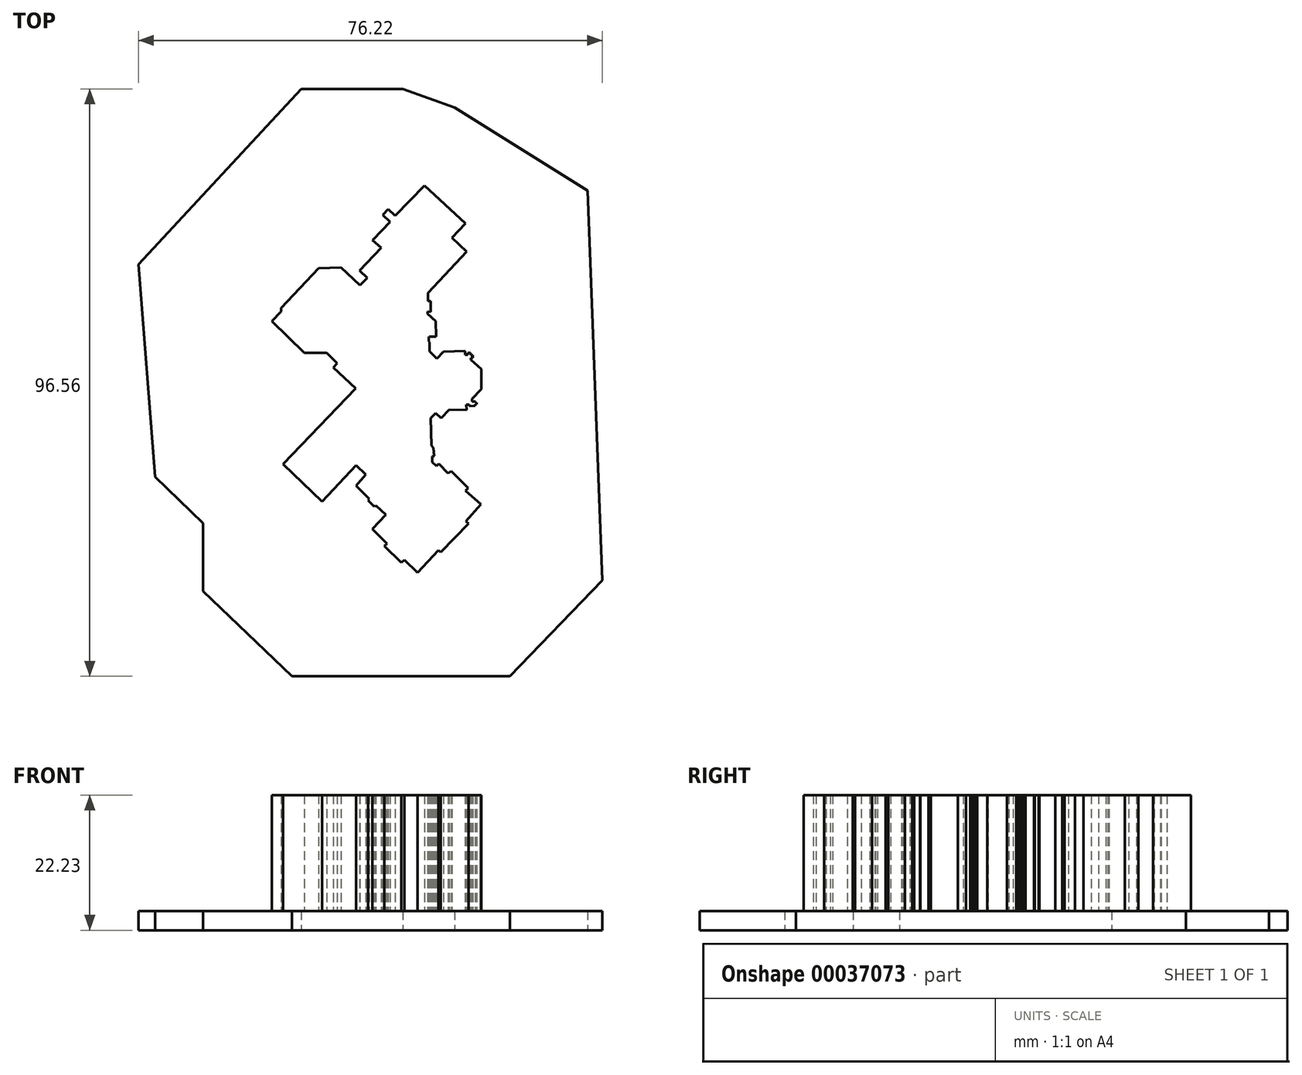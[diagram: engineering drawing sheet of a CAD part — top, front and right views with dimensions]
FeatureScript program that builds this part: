
annotation { "Feature Type Name" : "Feature", "Feature Type Description" : "" }
export const myFeature = defineFeature(function(context is Context, id is Id, definition is map)
    precondition{}
    {
        {
            var Q0;
            Q0=qCreatedBy(makeId("Top.planeOp"),FACE);
            var sketch = newSketch(context, id + "F0", { "sketchPlane" : qUnion([Q0])});
            skLineSegment(sketch, "E0", {"start": v(-23.08, 49.34) * mm, "end": v(-6.38, 49.34) * mm});
            skLineSegment(sketch, "E1", {"start": v(-6.38, 49.34) * mm, "end": v(2.13, 46.3) * mm});
            skLineSegment(sketch, "E2", {"start": v(2.13, 46.3) * mm, "end": v(23.99, 32.64) * mm});
            skLineSegment(sketch, "E3", {"start": v(23.99, 32.64) * mm, "end": v(26.42, -31.43) * mm});
            skLineSegment(sketch, "E4", {"start": v(26.42, -31.43) * mm, "end": v(11.23, -47.22) * mm});
            skLineSegment(sketch, "E5", {"start": v(11.23, -47.22) * mm, "end": v(-24.6, -47.22) * mm});
            skLineSegment(sketch, "E6", {"start": v(-24.6, -47.22) * mm, "end": v(-39.17, -33.25) * mm});
            skLineSegment(sketch, "E7", {"start": v(-39.17, -33.25) * mm, "end": v(-39.17, -22.01) * mm});
            skLineSegment(sketch, "E8", {"start": v(-39.17, -22.01) * mm, "end": v(-47.06, -14.42) * mm});
            skLineSegment(sketch, "E9", {"start": v(-47.06, -14.42) * mm, "end": v(-49.8, 20.5) * mm});
            skLineSegment(sketch, "E10", {"start": v(-49.8, 20.5) * mm, "end": v(-23.08, 49.34) * mm});
            skSolve(sketch);
        }
        {
            var Q0;
            Q0=makeQuery(id+"F0.imprint","IMPRINT",FACE,{"disambiguationData":[TD([[makeQuery(id+"F0.imprint","IMPRINT",EDGE,{"derivedFrom":sQuery(id+"F0.wireOp",EDGE,"E0")}),-1.0]])]});
            extrude(context, id + "F1", {"entities" : qUnion([Q0]), "depth" : 3.17 * mm});
        }
        {
            var Q0;
            Q0=makeQuery(id+"F1.opExtrude","CAP_FACE",FACE,{"disambiguationData":[OSD([sQuery(id+"F0.wireOp",EDGE,"E0"),sQuery(id+"F0.wireOp",EDGE,"E1"),sQuery(id+"F0.wireOp",EDGE,"E2"),sQuery(id+"F0.wireOp",EDGE,"E3"),sQuery(id+"F0.wireOp",EDGE,"E4"),sQuery(id+"F0.wireOp",EDGE,"E5"),sQuery(id+"F0.wireOp",EDGE,"E6"),sQuery(id+"F0.wireOp",EDGE,"E7"),sQuery(id+"F0.wireOp",EDGE,"E8"),sQuery(id+"F0.wireOp",EDGE,"E9"),sQuery(id+"F0.wireOp",EDGE,"E10")])],"isStart":false});
            var sketch = newSketch(context, id + "F2", { "sketchPlane" : qUnion([Q0])});
            skLineSegment(sketch, "E11", {"start": v(-11.23, 24.6) * mm, "end": v(-8.46, 27.47) * mm});
            skLineSegment(sketch, "E12", {"start": v(-8.46, 27.47) * mm, "end": v(-9.65, 28.61) * mm});
            skLineSegment(sketch, "E13", {"start": v(-9.65, 28.61) * mm, "end": v(-8.75, 29.55) * mm});
            skLineSegment(sketch, "E14", {"start": v(-8.75, 29.55) * mm, "end": v(-7.63, 28.48) * mm});
            skLineSegment(sketch, "E15", {"start": v(-7.63, 28.48) * mm, "end": v(-2.82, 33.47) * mm});
            skLineSegment(sketch, "E16", {"start": v(-2.82, 33.47) * mm, "end": v(3.93, 27.23) * mm});
            skLineSegment(sketch, "E17", {"start": v(3.93, 27.23) * mm, "end": v(1.74, 24.86) * mm});
            skLineSegment(sketch, "E18", {"start": v(1.74, 24.86) * mm, "end": v(4.13, 22.62) * mm});
            skLineSegment(sketch, "E19", {"start": v(4.13, 22.62) * mm, "end": v(-2.23, 15.81) * mm});
            skLineSegment(sketch, "E20", {"start": v(-2.23, 15.81) * mm, "end": v(-2.23, 14.44) * mm});
            skLineSegment(sketch, "E21", {"start": v(-2.23, 14.44) * mm, "end": v(-1.8, 14.44) * mm});
            skLineSegment(sketch, "E22", {"start": v(-1.8, 14.44) * mm, "end": v(-1.8, 12.7) * mm});
            skLineSegment(sketch, "E23", {"start": v(-1.8, 12.7) * mm, "end": v(-2.3, 12.75) * mm});
            skLineSegment(sketch, "E24", {"start": v(-2.3, 12.75) * mm, "end": v(-2.3, 12.35) * mm});
            skLineSegment(sketch, "E25", {"start": v(-2.3, 12.35) * mm, "end": v(-0.95, 11.18) * mm});
            skLineSegment(sketch, "E26", {"start": v(-0.95, 11.18) * mm, "end": v(-0.88, 8.63) * mm});
            skLineSegment(sketch, "E27", {"start": v(-0.88, 8.63) * mm, "end": v(-2.02, 8.6) * mm});
            skLineSegment(sketch, "E28", {"start": v(-2.02, 8.6) * mm, "end": v(-2.13, 8.49) * mm});
            skLineSegment(sketch, "E29", {"start": v(-2.13, 8.49) * mm, "end": v(-2.13, 7.83) * mm});
            skLineSegment(sketch, "E30", {"start": v(-2.13, 7.83) * mm, "end": v(-1.99, 7.7) * mm});
            skLineSegment(sketch, "E31", {"start": v(-1.99, 7.7) * mm, "end": v(-1.99, 6.24) * mm});
            skLineSegment(sketch, "E32", {"start": v(-1.99, 6.24) * mm, "end": v(-0.74, 5.03) * mm});
            skLineSegment(sketch, "E33", {"start": v(-0.74, 5.03) * mm, "end": v(0.32, 6.13) * mm});
            skLineSegment(sketch, "E34", {"start": v(0.32, 6.13) * mm, "end": v(3.84, 6.3) * mm});
            skLineSegment(sketch, "E35", {"start": v(3.84, 6.3) * mm, "end": v(3.88, 5.65) * mm});
            skLineSegment(sketch, "E36", {"start": v(3.88, 5.65) * mm, "end": v(4.32, 5.66) * mm});
            skLineSegment(sketch, "E37", {"start": v(4.32, 5.66) * mm, "end": v(4.32, 5.93) * mm});
            skLineSegment(sketch, "E38", {"start": v(4.32, 5.93) * mm, "end": v(4.79, 5.94) * mm});
            skLineSegment(sketch, "E39", {"start": v(4.79, 5.94) * mm, "end": v(4.8, 5.56) * mm});
            skLineSegment(sketch, "E40", {"start": v(4.8, 5.56) * mm, "end": v(5.15, 5.56) * mm});
            skLineSegment(sketch, "E41", {"start": v(5.15, 5.56) * mm, "end": v(5.15, 5.14) * mm});
            skLineSegment(sketch, "E42", {"start": v(5.15, 5.14) * mm, "end": v(4.85, 5.14) * mm});
            skLineSegment(sketch, "E43", {"start": v(4.85, 5.14) * mm, "end": v(4.85, 4.79) * mm});
            skLineSegment(sketch, "E44", {"start": v(4.85, 4.79) * mm, "end": v(6.54, 3.26) * mm});
            skLineSegment(sketch, "E45", {"start": v(6.54, 3.26) * mm, "end": v(6.54, 0) * mm});
            skLineSegment(sketch, "E46", {"start": v(6.54, 0) * mm, "end": v(5.01, -1.63) * mm});
            skLineSegment(sketch, "E47", {"start": v(5.01, -1.63) * mm, "end": v(5.01, -2.04) * mm});
            skLineSegment(sketch, "E48", {"start": v(5.01, -2.04) * mm, "end": v(5.58, -2.02) * mm});
            skLineSegment(sketch, "E49", {"start": v(5.58, -2.02) * mm, "end": v(5.59, -2.22) * mm});
            skLineSegment(sketch, "E50", {"start": v(5.59, -2.22) * mm, "end": v(5.78, -2.2) * mm});
            skLineSegment(sketch, "E51", {"start": v(5.78, -2.2) * mm, "end": v(5.79, -2.5) * mm});
            skLineSegment(sketch, "E52", {"start": v(5.79, -2.5) * mm, "end": v(5.53, -2.5) * mm});
            skLineSegment(sketch, "E53", {"start": v(5.53, -2.5) * mm, "end": v(5.53, -2.76) * mm});
            skLineSegment(sketch, "E54", {"start": v(5.53, -2.76) * mm, "end": v(4.55, -2.8) * mm});
            skLineSegment(sketch, "E55", {"start": v(4.55, -2.8) * mm, "end": v(4.54, -2.55) * mm});
            skLineSegment(sketch, "E56", {"start": v(4.54, -2.55) * mm, "end": v(4.1, -2.56) * mm});
            skLineSegment(sketch, "E57", {"start": v(4.1, -2.56) * mm, "end": v(4.12, -3.46) * mm});
            skLineSegment(sketch, "E58", {"start": v(4.12, -3.46) * mm, "end": v(1.28, -3.39) * mm});
            skLineSegment(sketch, "E59", {"start": v(1.28, -3.39) * mm, "end": v(-0.08, -4.79) * mm});
            skLineSegment(sketch, "E60", {"start": v(-0.08, -4.79) * mm, "end": v(-0.96, -3.94) * mm});
            skLineSegment(sketch, "E61", {"start": v(-0.96, -3.94) * mm, "end": v(-1.76, -4.75) * mm});
            skLineSegment(sketch, "E62", {"start": v(-1.76, -4.75) * mm, "end": v(-1.64, -9.28) * mm});
            skLineSegment(sketch, "E63", {"start": v(-1.64, -9.28) * mm, "end": v(-1.32, -9.64) * mm});
            skLineSegment(sketch, "E64", {"start": v(-1.32, -9.64) * mm, "end": v(-1.21, -11) * mm});
            skLineSegment(sketch, "E65", {"start": v(-1.21, -11) * mm, "end": v(-1.51, -11.05) * mm});
            skLineSegment(sketch, "E66", {"start": v(-1.51, -11.05) * mm, "end": v(-1.51, -12) * mm});
            skLineSegment(sketch, "E67", {"start": v(-1.51, -12) * mm, "end": v(-0.81, -12.66) * mm});
            skLineSegment(sketch, "E68", {"start": v(-0.81, -12.66) * mm, "end": v(-0.45, -12.3) * mm});
            skLineSegment(sketch, "E69", {"start": v(-0.45, -12.3) * mm, "end": v(1.1, -13.84) * mm});
            skLineSegment(sketch, "E70", {"start": v(1.1, -13.84) * mm, "end": v(1.6, -13.5) * mm});
            skLineSegment(sketch, "E71", {"start": v(1.6, -13.5) * mm, "end": v(4.36, -16.25) * mm});
            skLineSegment(sketch, "E72", {"start": v(4.36, -16.25) * mm, "end": v(3.96, -16.7) * mm});
            skLineSegment(sketch, "E73", {"start": v(3.96, -16.7) * mm, "end": v(6.46, -18.91) * mm});
            skLineSegment(sketch, "E74", {"start": v(6.46, -18.91) * mm, "end": v(3.98, -21.7) * mm});
            skLineSegment(sketch, "E75", {"start": v(3.98, -21.7) * mm, "end": v(4.41, -22.09) * mm});
            skLineSegment(sketch, "E76", {"start": v(4.41, -22.09) * mm, "end": v(-0.1, -26.8) * mm});
            skLineSegment(sketch, "E77", {"start": v(-0.1, -26.8) * mm, "end": v(-0.5, -26.47) * mm});
            skLineSegment(sketch, "E78", {"start": v(-0.5, -26.47) * mm, "end": v(-3.92, -30.15) * mm});
            skLineSegment(sketch, "E79", {"start": v(-3.92, -30.15) * mm, "end": v(-6.12, -28.1) * mm});
            skLineSegment(sketch, "E80", {"start": v(-6.12, -28.1) * mm, "end": v(-6.61, -28.54) * mm});
            skLineSegment(sketch, "E81", {"start": v(-6.61, -28.54) * mm, "end": v(-9.37, -25.76) * mm});
            skLineSegment(sketch, "E82", {"start": v(-9.37, -25.76) * mm, "end": v(-8.97, -25.4) * mm});
            skLineSegment(sketch, "E83", {"start": v(-8.97, -25.4) * mm, "end": v(-11.38, -22.99) * mm});
            skLineSegment(sketch, "E84", {"start": v(-11.38, -22.99) * mm, "end": v(-9.16, -20.66) * mm});
            skLineSegment(sketch, "E85", {"start": v(-9.16, -20.66) * mm, "end": v(-10.8, -19.1) * mm});
            skLineSegment(sketch, "E86", {"start": v(-10.8, -19.1) * mm, "end": v(-11.04, -19.3) * mm});
            skLineSegment(sketch, "E87", {"start": v(-11.04, -19.3) * mm, "end": v(-12.05, -18.32) * mm});
            skLineSegment(sketch, "E88", {"start": v(-12.05, -18.32) * mm, "end": v(-11.84, -18.04) * mm});
            skLineSegment(sketch, "E89", {"start": v(-11.84, -18.04) * mm, "end": v(-14.06, -15.87) * mm});
            skLineSegment(sketch, "E90", {"start": v(-14.06, -15.87) * mm, "end": v(-12.45, -14.07) * mm});
            skLineSegment(sketch, "E91", {"start": v(-12.45, -14.07) * mm, "end": v(-14.04, -12.54) * mm});
            skLineSegment(sketch, "E92", {"start": v(-14.04, -12.54) * mm, "end": v(-19.64, -18.49) * mm});
            skLineSegment(sketch, "E93", {"start": v(-19.64, -18.49) * mm, "end": v(-26, -12.36) * mm});
            skLineSegment(sketch, "E94", {"start": v(-26, -12.36) * mm, "end": v(-14.11, 0.13) * mm});
            skLineSegment(sketch, "E95", {"start": v(-14.11, 0.13) * mm, "end": v(-17.8, 3.56) * mm});
            skLineSegment(sketch, "E96", {"start": v(-17.8, 3.56) * mm, "end": v(-17.14, 4.27) * mm});
            skLineSegment(sketch, "E97", {"start": v(-17.14, 4.27) * mm, "end": v(-18.85, 5.93) * mm});
            skLineSegment(sketch, "E98", {"start": v(-18.85, 5.93) * mm, "end": v(-22.52, 5.93) * mm});
            skLineSegment(sketch, "E99", {"start": v(-22.52, 5.93) * mm, "end": v(-27.89, 11.14) * mm});
            skLineSegment(sketch, "E100", {"start": v(-27.89, 11.14) * mm, "end": v(-26.32, 12.76) * mm});
            skLineSegment(sketch, "E101", {"start": v(-26.32, 12.76) * mm, "end": v(-26.36, 13.33) * mm});
            skLineSegment(sketch, "E102", {"start": v(-26.36, 13.33) * mm, "end": v(-20.17, 19.86) * mm});
            skLineSegment(sketch, "E103", {"start": v(-20.17, 19.86) * mm, "end": v(-16.54, 20) * mm});
            skLineSegment(sketch, "E104", {"start": v(-16.54, 20) * mm, "end": v(-13.4, 17.1) * mm});
            skLineSegment(sketch, "E105", {"start": v(-13.4, 17.1) * mm, "end": v(-12.22, 18.29) * mm});
            skLineSegment(sketch, "E106", {"start": v(-12.22, 18.29) * mm, "end": v(-13.44, 19.5) * mm});
            skLineSegment(sketch, "E107", {"start": v(-13.44, 19.5) * mm, "end": v(-9.91, 23.24) * mm});
            skLineSegment(sketch, "E108", {"start": v(-9.91, 23.24) * mm, "end": v(-11.35, 24.52) * mm});
            skLineSegment(sketch, "E109", {"start": v(-11.35, 24.52) * mm, "end": v(-11.23, 24.6) * mm});
            skSolve(sketch);
        }
        {
            var Q0;
            Q0=makeQuery(id+"F2.imprint","IMPRINT",FACE,{"disambiguationData":[TD([[makeQuery(id+"F2.imprint","IMPRINT",EDGE,{"derivedFrom":sQuery(id+"F2.wireOp",EDGE,"E11")}),-1.0]])]});
            extrude(context, id + "F3", {"entities" : qUnion([Q0]), "operationType" : NewBodyOperationType.ADD, "depth" : 19.05 * mm});
        }
    });
